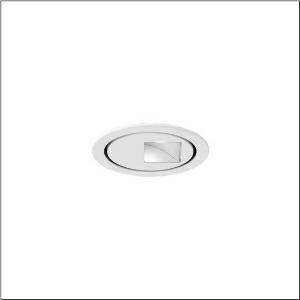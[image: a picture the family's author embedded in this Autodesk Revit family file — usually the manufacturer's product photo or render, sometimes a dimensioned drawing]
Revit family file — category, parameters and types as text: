
# Revit family: lunis_11_micro_round_51dj11cd1wn21
name_source: partatom
category: Lighting Fixtures
units: mm (PartAtom-declared; Revit-internal decimal feet)

## family parameters
Cut with Voids When Loaded = No
Host = Face
Light Source = No
Part Type = Normal
Room Calculation Point = No
Round Connector Dimension = Use Diameter
Shared = No

## types (1)
- Lunis 11 micro round (1 x LED 4000K / CRI = 90 (unbekannt), 1210 lm, 4000K)
    Apparent Load = 20 VA
    CIE Flux Codes = 42 75 96 100 100
    Color Rendering = 90
    Color Temperature = 4000K
    Default Elevation = 1800 mm
    Description = Lunis 11 micro round, downlight, light control with wallwasher, of highly reflective aluminium, highly specular, light emission: direct distribution, LED rated luminous flux: 1.210lm, light colour: 940, with terminal, 5-pole, mains connection: 220..230V, AC, 50/60Hz, LED module, of aluminium, highly specular, white, diameter: 114mm, clamping range: 1..40mm, recessing ring, of plastic, traffic white (RAL 9016), protection rating (complete): IP20, insulation class (complete): insulation class II (safety insulation), certification: CE, permissible ambient temperature for indoor applications: 0..+35°C, packaging unit: 1 piece
    Height = 0 mm  [stored 0 ft]
    Lamp = 1 x LED 4000K / CRI >= 90 (unbekannt)
    Lamp Light Flux = 1210 lm
    Lamp count = 1
    Length = 114 mm
    Luminous efficacy = 61 lm/W
    Manufacturer = Siteco
    ModVariant = No
    Model = 51DJ11CD1WN21
    Mounting Place = Ceiling
    Mounting Type = Recessed
    Number of Poles = 1
    OnlyDefault = Yes
    Power Factor = 1
    Product Name = Lunis 11 micro round
    Product group = downlight
    ProductGroupID = 401
    Protection Class = Protection class II
    Protection Degree = IP 20
    RLX_Detail_Level = 1
    RLX_Emergency_Light_Flux = 0 lm
    RLX_Emergency_Type = 0
    RLX_Emergency_Type_DB = No
    RlxData = <blob elided: 40121 chars, md5=7be16823>
    Socket = socket
    Standby Power = 0 W
    System Light Flux = 1210 lm
    System Power = 20 W
    Type Comments = Product without accessories
    Type Image = l_1004773.jpg
    URL = http://relux.com
    VarID = ---
    Voltage = 0 V
    Weight = 0.00 kg
    Width = 114 mm

note: [stored X ft] marks values corroborated as IEEE doubles in the binary element streams (Revit-internal decimal feet)

## geometry (parser evidence)
native form markers: Blend x4, Sweep x10
no freeform markers — native parametric forms only
